# Revit family: Sink_Wall_Hung _Surgeon _Scrub-Elkay-EWSF26026_2_KWC_KWSC_SACC
name_source: partatom
category: Plumbing Fixtures
units: mm (PartAtom-declared; Revit-internal decimal feet)

## family parameters
Cut with Voids When Loaded = No
Host = Face
Maintain Annotation Orientation = No
OmniClass Number = 23.45.05.14.14.21
OmniClass Title = Surgeons Scrub-Up Sinks
Part Type = Normal
Room Calculation Point = No
Round Connector Dimension = Use Diameter
Shared = No

## types (4) — shared parameters
Assembly Code = D2010.60
Bowl 1 Dimensions = 28 inch x 16 1/4 inch x 11 inch
Bowl 2 Dimensions = 28 inch x 16 1/4 inch x 11 inch
Default Elevation = 48.00"
Description = Stainless Steel 60 inch x 23 inch x 26 inch Wall Hung Double Station Surgeon Scrub Sink Kit
Drain Size = 3 1/2 inch
Main Material = Finish-Elkay-Stainless Steel
Manufacturer = Elkay Manufacturer Company
Manufacturer Brand = Elkay (by Zurn Elkay Water Solutions)
No of Bowls = 2
Outlet Connection Size (inch) = 1.50"
Product Documentation Link = https://www.elkayfiles.com
Product Installation Sheet URL = https://www.elkayfiles.com
Product Page URL = https://www.elkay.com
Product data URL = https://www.bimobject.com
Repair Parts URL = https://www.elkayfiles.com
Sink Dimensions = 60 inch x 23 inch x 26 inch
Sink Height = 26.00"
Sink Length = 60.00"
Sink Width = 23.00"
URL = https://www.elkay.com

## per-type parameters (varying)
| type | Approx. Shipping Weight (lbs) | Bottom shroud | Hole | LK394A | LKB721C | Model | Product Weight (lbs) | Soap panel | Soap spout | Temperature handle | Water panel |
| EWSF260262 (Wall Hung Double Station Surgeon Scrub Sink) | 200 | No | Yes | No | No | EWSF260262 | 140 | No | No | No | No |
| EWSF26026KWC (Wall Hung Double Station Surgeon Scrub Sink Kit) | 150 | Yes | No | Yes | No | EWSF26026KWC | 140 | No | No | Yes | Yes |
| EWSF26026SACC (Wall Hung Double Station Surgeon Scrub Sink Kit) | 172 | No | No | No | Yes | EWSF26026SACC | 162 | No | No | No | No |
| EWSF26026KWSC (Wall Hung Double Station Surgeon Scrub Sink Kit) | 150 | Yes | No | Yes | No | EWSF26026KWSC | 140 | Yes | Yes | Yes | Yes |

## geometry (parser evidence)
native form markers: Sweep x31
no freeform markers — native parametric forms only
